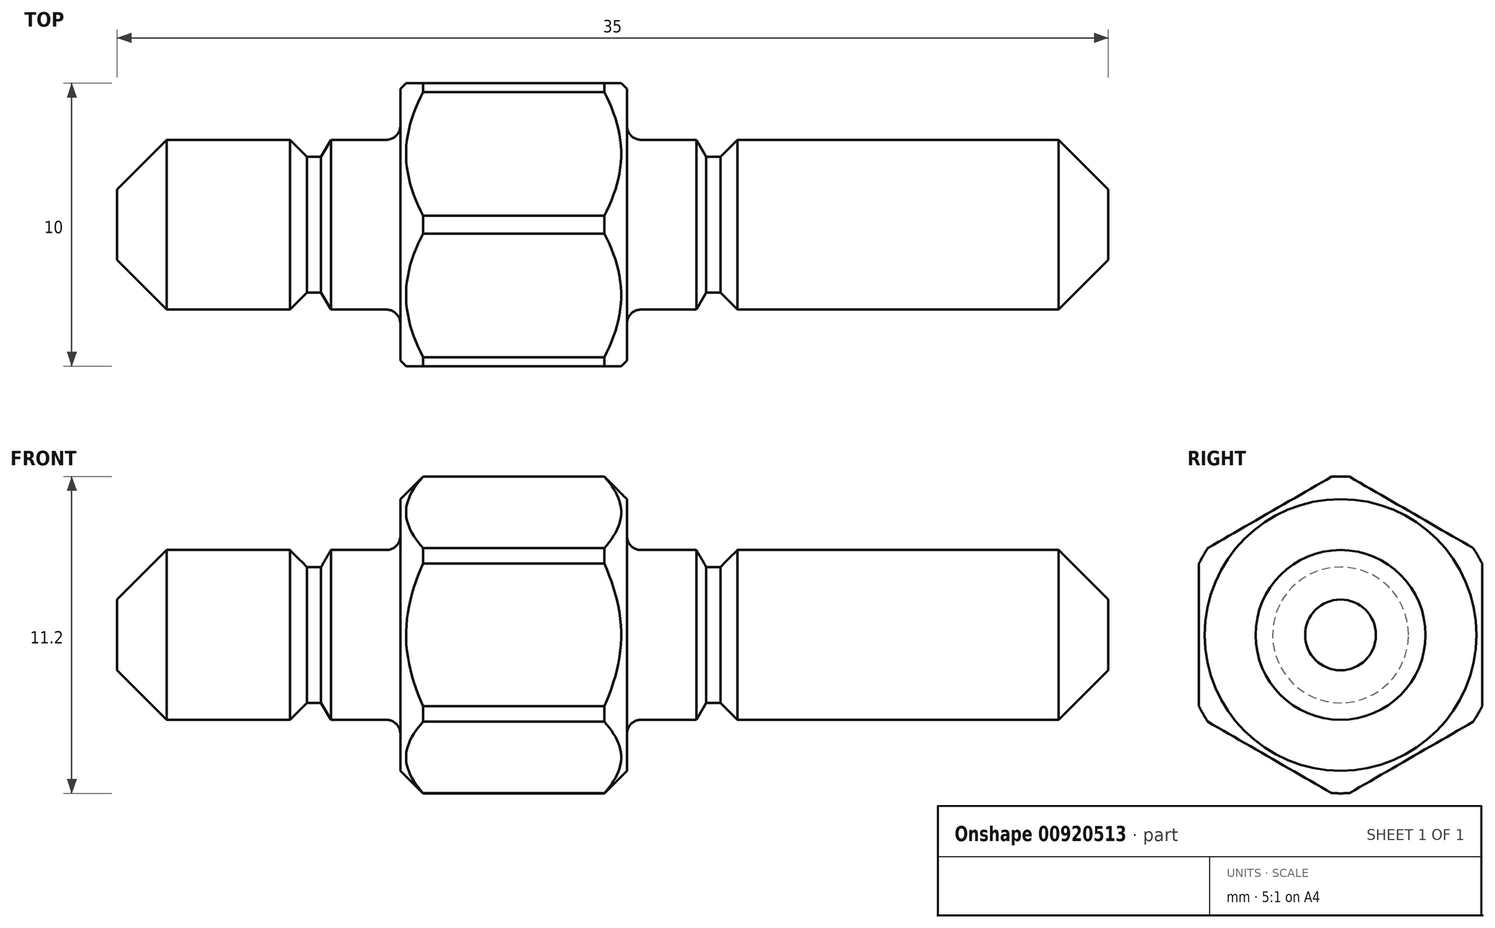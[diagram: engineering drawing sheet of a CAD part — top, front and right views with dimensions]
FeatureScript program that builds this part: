
annotation { "Feature Type Name" : "Feature", "Feature Type Description" : "" }
export const myFeature = defineFeature(function(context is Context, id is Id, definition is map)
    precondition{}
    {
        {
            var Q0;
            Q0=qCreatedBy(makeId("Front.planeOp"),FACE);
            var sketch = newSketch(context, id + "F0", { "sketchPlane" : qUnion([Q0])});
            skLineSegment(sketch, "E0", {"start": v(-65, 0) * mm, "end": v(65, 0) * mm, "construction": true});
            skLineSegment(sketch, "E1", {"start": v(0, 10.6) * mm, "end": v(0, -10.6) * mm, "construction": true});
            skLineSegment(sketch, "E2", {"start": v(21, 0) * mm, "end": v(-14, 0) * mm});
            skLineSegment(sketch, "E3", {"start": v(-14, 0) * mm, "end": v(-14, 1.25) * mm});
            skLineSegment(sketch, "E4", {"start": v(-12.25, 3) * mm, "end": v(-7.9, 3) * mm});
            skLineSegment(sketch, "E5", {"start": v(-4, 3) * mm, "end": v(-4, 4.8) * mm});
            skLineSegment(sketch, "E6", {"start": v(-3.2, 5.6) * mm, "end": v(3.2, 5.6) * mm});
            skLineSegment(sketch, "E7", {"start": v(4, 4.8) * mm, "end": v(4, 3) * mm});
            skLineSegment(sketch, "E8", {"start": v(7.9, 3) * mm, "end": v(19.25, 3) * mm});
            skLineSegment(sketch, "E9", {"start": v(21, 1.25) * mm, "end": v(21, 0) * mm});
            skLineSegment(sketch, "E10", {"start": v(-4, 3) * mm, "end": v(-6.45, 3) * mm});
            skLineSegment(sketch, "E11", {"start": v(4, 3) * mm, "end": v(6.45, 3) * mm});
            skLineSegment(sketch, "E12", {"start": v(-14, 1.25) * mm, "end": v(-12.25, 3) * mm});
            skLineSegment(sketch, "E13", {"start": v(-4, 4.8) * mm, "end": v(-3.2, 5.6) * mm});
            skLineSegment(sketch, "E14", {"start": v(4, 4.8) * mm, "end": v(3.2, 5.6) * mm});
            skLineSegment(sketch, "E15", {"start": v(21, 1.25) * mm, "end": v(19.25, 3) * mm});
            skLineSegment(sketch, "E16", {"start": v(-6.8, 2.4) * mm, "end": v(-7.3, 2.4) * mm});
            skLineSegment(sketch, "E17", {"start": v(6.8, 2.4) * mm, "end": v(7.3, 2.4) * mm});
            skLineSegment(sketch, "E18", {"start": v(-7.3, 2.4) * mm, "end": v(-7.9, 3) * mm});
            skLineSegment(sketch, "E19", {"start": v(7.3, 2.4) * mm, "end": v(7.9, 3) * mm});
            skLineSegment(sketch, "E20", {"start": v(-6.45, 3) * mm, "end": v(-6.8, 2.4) * mm});
            skLineSegment(sketch, "E21", {"start": v(6.8, 2.4) * mm, "end": v(6.45, 3) * mm});
            skLineSegment(sketch, "E22", {"start": v(-7.3, 2.4) * mm, "end": v(-12.85, 2.4) * mm});
            skLineSegment(sketch, "E23", {"start": v(7.3, 2.4) * mm, "end": v(19.85, 2.4) * mm});
            skSolve(sketch);
        }
        {
            var Q0;
            Q0 = qSketchRegion(id + "F0", true);
            var Q1;
            Q1=sQuery(id+"F0.wireOp",EDGE,"E0");
            revolve(context, id + "F1", {"surfaceOperationType" : NewSurfaceOperationType.NEW, "entities" : qUnion([Q0]), "axis" : qUnion([Q1]), "revolveType" : RevolveType.FULL});
        }
        {
            var Q0;
            Q0=qCreatedBy(makeId("Right.planeOp"),FACE);
            var sketch = newSketch(context, id + "F2", { "sketchPlane" : qUnion([Q0])});
            skCircle(sketch, "E24.cCircle", {"center": v(0, 0) * mm, "radius": 5.77 * mm, "construction": true});
            skLineSegment(sketch, "E24.0", {"start": v(0, -5.77) * mm, "end": v(-5, -2.89) * mm});
            skLineSegment(sketch, "E24.1", {"start": v(-5, -2.89) * mm, "end": v(-5, 2.89) * mm});
            skLineSegment(sketch, "E24.2", {"start": v(-5, 2.89) * mm, "end": v(0, 5.77) * mm});
            skLineSegment(sketch, "E24.3", {"start": v(0, 5.77) * mm, "end": v(5, 2.89) * mm});
            skLineSegment(sketch, "E24.4", {"start": v(5, 2.89) * mm, "end": v(5, -2.89) * mm});
            skLineSegment(sketch, "E24.5", {"start": v(5, -2.89) * mm, "end": v(0, -5.77) * mm});
            skLineSegment(sketch, "E25", {"start": v(12.5, 0) * mm, "end": v(-12.5, 0) * mm, "construction": true});
            skLineSegment(sketch, "E26", {"start": v(0, 12.5) * mm, "end": v(0, -12.5) * mm, "construction": true});
            skCircle(sketch, "E27", {"center": v(0, 0) * mm, "radius": 12.5 * mm});
            skSolve(sketch);
        }
        {
            var Q0;
            Q0 = qSketchRegion(id + "F2", true);
            extrude(context, id + "F3", {"entities" : qUnion([Q0]), "operationType" : NewBodyOperationType.REMOVE, "endBound" : BoundingType.SYMMETRIC, "oppositeDirection" : true, "depth" : 25 * mm, "offsetDistance" : 25 * mm});
        }
        {
            var Q0;
            Q0=makeQuery(id+"F1.opRevolve","SWEPT_EDGE",EDGE,{"disambiguationData":[OSD([sQuery(id+"F0.wireOp",EDGE,"E5"),sQuery(id+"F0.wireOp",EDGE,"E10")])]});
            var Q1;
            Q1=makeQuery(id+"F1.opRevolve","SWEPT_EDGE",EDGE,{"disambiguationData":[OSD([sQuery(id+"F0.wireOp",EDGE,"E7"),sQuery(id+"F0.wireOp",EDGE,"E11")])]});
            fillet(context, id + "F4", {"entities" : qUnion([Q0, Q1]), "radius" : .5 * mm, "tangentPropagation" : true, "allowEdgeOverflow" : false});
        }
        {
            var Q0;
            Q0=sQuery(id+"F0.wireOp",EDGE,"E22");
            var Q1;
            Q1=sQuery(id+"F0.wireOp",EDGE,"E23");
            var Q2;
            Q2=sQuery(id+"F0.wireOp",EDGE,"E0");
            revolve(context, id + "F5", {"bodyType" : ToolBodyType.SURFACE, "surfaceOperationType" : NewSurfaceOperationType.NEW, "surfaceEntities" : qUnion([Q0, Q1]), "axis" : qUnion([Q2]), "revolveType" : RevolveType.FULL});
        }
    });
